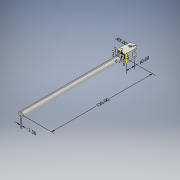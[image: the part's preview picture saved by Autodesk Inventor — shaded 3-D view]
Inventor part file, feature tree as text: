
AUTODESK INVENTOR PART (.ipt)
format: ipt  version: 2018 (Build 220112000, 112)  size: 156,160 bytes
history: native  units: mm
features: other x5, extrude x4, sketch x3, hole x1
ambient origin geometry x8: Origin, YZ Plane, XZ Plane, XY Plane, X Axis, Y Axis, Z Axis, Center Point
bodies: Solide1 (feature_tree)
feature tree (13):
  other  "Annotations"
  extrude  "Extrusion1"  Depth=10.0mm
  hole  "Perçage1"  [1 undecoded]
  extrude  "Extrusion3"  Depth=10.0mm TaperAngle=0.0deg
  sketch  "Esquisse4"
  extrude  "Extrusion4"  Depth=10.0mm
  extrude  "Extrusion5"  Depth=100.0mm TaperAngle=0.0deg
  sketch  "Esquisse1"
  sketch  "Esquisse3"
  other  "Cote linéaire 1"
  other  "Cote linéaire 2"
  other  "Cote de rayon 1"
  other  "Cote linéaire 3"
note: 1 required parameter value undecoded (feature->parameter linkage not recoverable at this tier; creation-order binding heuristic only, values carry confidence <= 0.55)
